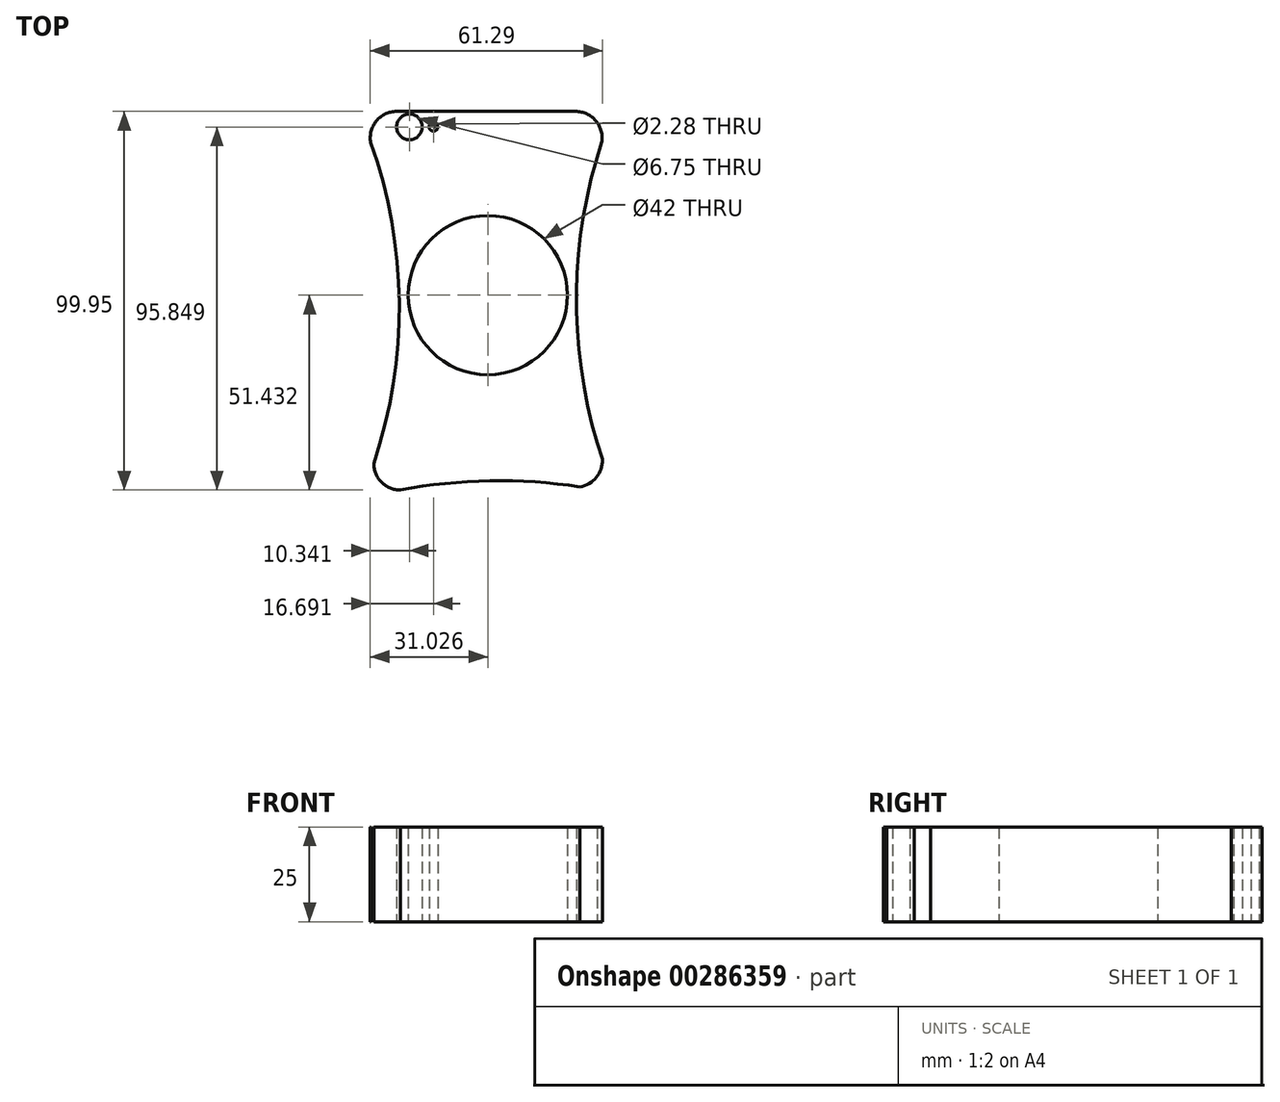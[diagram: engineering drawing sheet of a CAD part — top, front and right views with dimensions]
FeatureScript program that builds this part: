
annotation { "Feature Type Name" : "Feature", "Feature Type Description" : "" }
export const myFeature = defineFeature(function(context is Context, id is Id, definition is map)
    precondition{}
    {
        {
            var Q0;
            Q0=qCreatedBy(makeId("Top.planeOp"),FACE);
            var sketch = newSketch(context, id + "F0", { "sketchPlane" : qUnion([Q0])});
            skLineSegment(sketch, "E0", {"start": v(-32.7, 29.53) * mm, "end": v(14.5, 29.53) * mm});
            skArc(sketch, "E1.filletArc", {"start": v(21.4, 21.33) * mm, "mid": v(19.86, 27.03) * mm, "end": v(14.5, 29.53) * mm});
            skArc(sketch, "E2.filletArc", {"start": v(15.62, -69.6) * mm, "mid": v(20, -67.1) * mm, "end": v(21.58, -62.32) * mm});
            skPoint(sketch, "E3.visualSharp", {"position": v(-38.4, -70.47) * mm});
            skArc(sketch, "E3.filletArc", {"start": v(-38.78, -63.42) * mm, "mid": v(-36.73, -68.37) * mm, "end": v(-31.78, -70.42) * mm});
            skPoint(sketch, "E4.visualSharp", {"position": v(-38.4, 29.53) * mm});
            skArc(sketch, "E4.filletArc", {"start": v(-32.7, 29.53) * mm, "mid": v(-38.07, 27.03) * mm, "end": v(-39.6, 21.33) * mm});
            skArc(sketch, "E5", {"start": v(21.4, 21.33) * mm, "mid": v(14.71, -20.51) * mm, "end": v(21.58, -62.32) * mm});
            skPoint(sketch, "E5.third.point", {"position": v(18.97, 13.1) * mm});
            skArc(sketch, "E6", {"start": v(-38.78, -63.42) * mm, "mid": v(-32.05, -20.98) * mm, "end": v(-39.6, 21.33) * mm});
            skPoint(sketch, "E6.third.point", {"position": v(-33.64, -42.48) * mm});
            skArc(sketch, "E7", {"start": v(15.62, -69.6) * mm, "mid": v(-8.11, -68) * mm, "end": v(-31.78, -70.42) * mm});
            skLineSegment(sketch, "E8", {"start": v(20.2, -57.97) * mm, "end": v(21.58, -62.32) * mm});
            skLineSegment(sketch, "E9", {"start": v(20.8, -59.86) * mm, "end": v(20.78, -59.86) * mm});
            skPoint(sketch, "E10.start.orphan", {"position": v(-30.67, -20.42) * mm});
            skLineSegment(sketch, "E11", {"start": v(-39.6, 21.33) * mm, "end": v(21.4, 21.33) * mm});
            skCircle(sketch, "E12", {"center": v(-29.37, 25.43) * mm, "radius": 3.38 * mm});
            skCircle(sketch, "E13", {"center": v(-23.02, 25.43) * mm, "radius": 1.14 * mm});
            skLineSegment(sketch, "E14.trimOffspring", {"start": v(-26, 25.43) * mm, "end": v(-32.75, 25.43) * mm});
            skPoint(sketch, "E15.start.orphan", {"position": v(-9.1, 29.53) * mm});
            skCircle(sketch, "E16", {"center": v(-8.68, -18.99) * mm, "radius": 21 * mm});
            skCircle(sketch, "E17", {"center": v(-8.68, -18.99) * mm, "radius": 13.5 * mm});
            skCircle(sketch, "E18", {"center": v(-8.68, -18.99) * mm, "radius": 8.5 * mm});
            skCircle(sketch, "E19", {"center": v(-8.68, -18.99) * mm, "radius": 3 * mm});
            skSolve(sketch);
        }
        {
            var Q0;
            Q0 = qSketchRegion(id + "F0", true);
            extrude(context, id + "F1", {"entities" : qUnion([Q0]), "depth" : 25 * mm});
        }
    });
